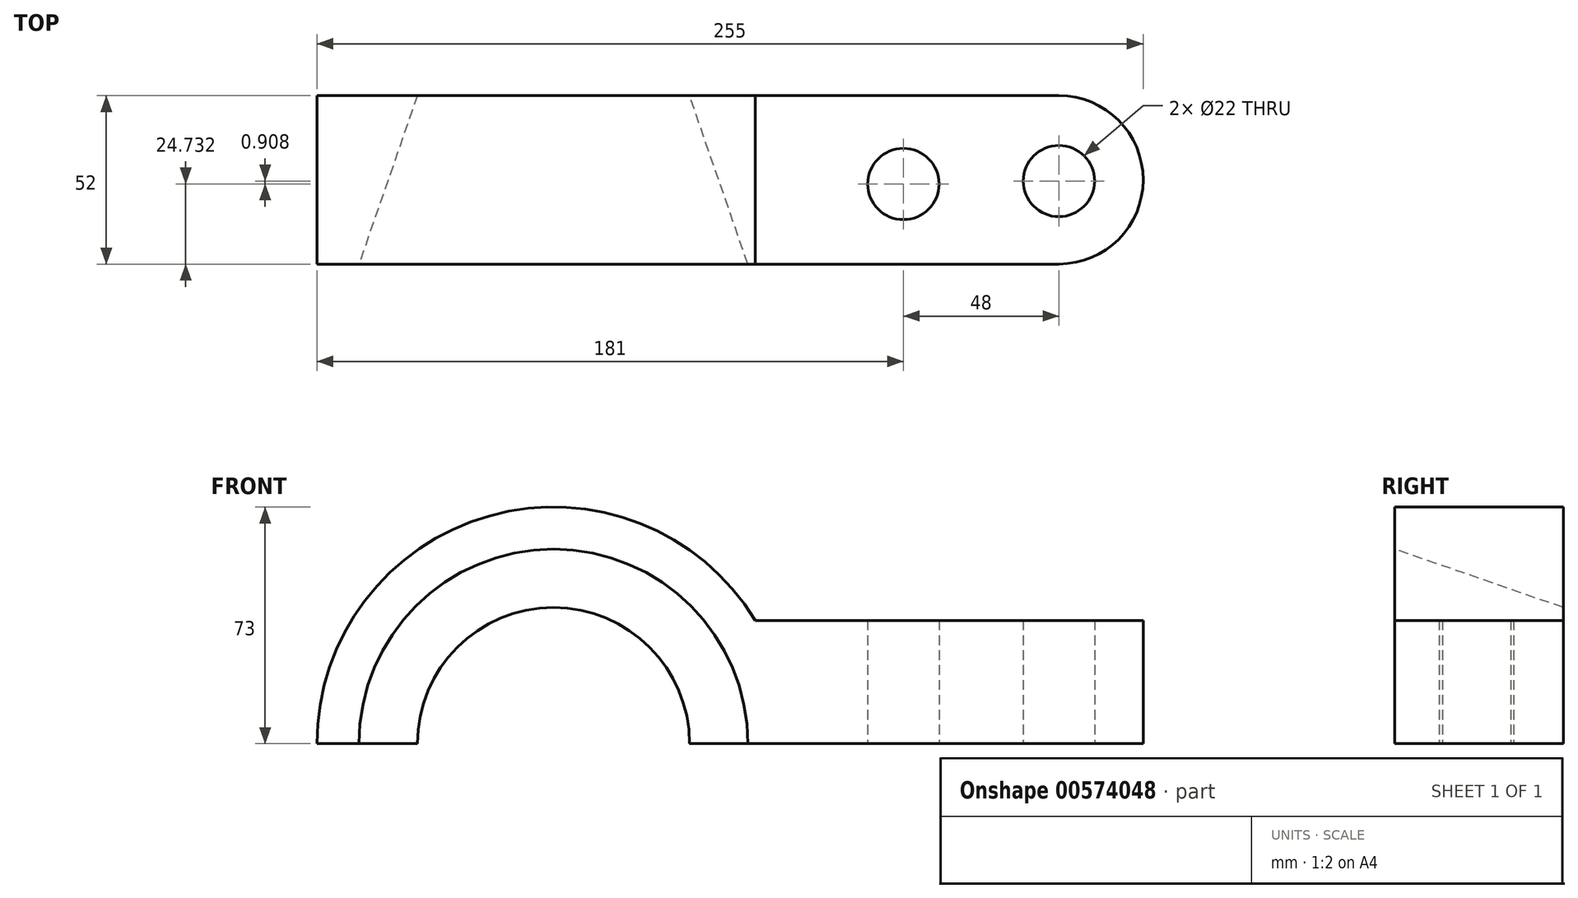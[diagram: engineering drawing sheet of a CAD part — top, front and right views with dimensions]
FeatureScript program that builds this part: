
annotation { "Feature Type Name" : "Feature", "Feature Type Description" : "" }
export const myFeature = defineFeature(function(context is Context, id is Id, definition is map)
    precondition{}
    {
        {
            var Q0;
            Q0=qCreatedBy(makeId("Front.planeOp"),FACE);
            var sketch = newSketch(context, id + "F0", { "sketchPlane" : qUnion([Q0])});
            skArc(sketch, "E0", {"start": v(42, 0) * mm, "mid": v(0, 42) * mm, "end": v(-42, 0) * mm});
            skArc(sketch, "E1", {"start": v(62.33, 38) * mm, "mid": v(-19.73, 70.28) * mm, "end": v(-73, 0) * mm});
            skLineSegment(sketch, "E2", {"start": v(-73, 0) * mm, "end": v(-42, 0) * mm});
            skLineSegment(sketch, "E3.trimOffspring", {"start": v(42, 0) * mm, "end": v(73, 0) * mm});
            skLineSegment(sketch, "E4", {"start": v(62.33, 38) * mm, "end": v(182, 38) * mm});
            skLineSegment(sketch, "E5", {"start": v(182, 38) * mm, "end": v(182, 0) * mm});
            skLineSegment(sketch, "E6", {"start": v(182, 0) * mm, "end": v(73, 0) * mm});
            skSolve(sketch);
        }
        {
            var Q0;
            Q0=makeQuery(id+"F0.imprint","IMPRINT",FACE,{"disambiguationData":[TD([[makeQuery(id+"F0.imprint","IMPRINT",EDGE,{"derivedFrom":sQuery(id+"F0.wireOp",EDGE,"E0")}),-1.0]])]});
            extrude(context, id + "F1", {"entities" : qUnion([Q0]), "depth" : 52 * mm, "offsetDistance" : 25 * mm});
        }
        {
            var Q0;
            Q0=makeQuery(id+"F1.opExtrude","SWEPT_FACE",FACE,{"disambiguationData":[OSD([sQuery(id+"F0.wireOp",EDGE,"E2")])]});
            var sketch = newSketch(context, id + "F2", { "sketchPlane" : qUnion([Q0])});
            skLineSegment(sketch, "E7", {"start": v(-60, 52) * mm, "end": v(-42, 0) * mm});
            skLineSegment(sketch, "E8", {"start": v(-42, 0) * mm, "end": v(-42, 52) * mm});
            skLineSegment(sketch, "E9", {"start": v(-42, 52) * mm, "end": v(-60, 52) * mm});
            skLineSegment(sketch, "E10", {"start": v(0, 53.19) * mm, "end": v(0, 0) * mm});
            skSolve(sketch);
        }
        {
            var Q0;
            Q0 = qSketchRegion(id + "F2", true);
            var Q1;
            Q1=sQuery(id+"F2.wireOp",EDGE,"E10");
            revolve(context, id + "F3", {"operationType" : NewBodyOperationType.REMOVE, "entities" : qUnion([Q0]), "axis" : qUnion([Q1]), "revolveType" : RevolveType.FULL});
        }
        {
            var Q0;
            Q0=makeQuery(id+"F1.opExtrude","SWEPT_FACE",FACE,{"disambiguationData":[OSD([sQuery(id+"F0.wireOp",EDGE,"E3.trimOffspring"),sQuery(id+"F0.wireOp",EDGE,"E6")])]});
            var sketch = newSketch(context, id + "F4", { "sketchPlane" : qUnion([Q0])});
            skSolve(sketch);
        }
        {
            var Q0;
            {var subQ0=sQuery(id+"F0.wireOp",EDGE,"E6");Q0=makeQuery(id+"F4.imprint","IMPRINT",FACE,{"disambiguationData":[TD([[makeQuery(id+"F4.imprint","IMPRINT",EDGE,{"derivedFrom":makeQuery(id+"F1.opExtrude","SWEPT_EDGE",EDGE,{"disambiguationData":[OSD([sQuery(id+"F0.wireOp",EDGE,"E5"),subQ0])]})}),-1.0]])]});}
            var sketch = newSketch(context, id + "F5", { "sketchPlane" : qUnion([Q0])});
            skCircle(sketch, "E11", {"center": v(108, 27.27) * mm, "radius": 11 * mm});
            skCircle(sketch, "E12", {"center": v(156, 26.36) * mm, "radius": 11 * mm});
            skSolve(sketch);
        }
        {
            var Q0;
            Q0=makeQuery(id+"F5.imprint","IMPRINT",FACE,{"disambiguationData":[TD([[makeQuery(id+"F5.imprint","IMPRINT",EDGE,{"derivedFrom":sQuery(id+"F5.wireOp",EDGE,"E12")}),1.0]])]});
            var Q1;
            Q1=makeQuery(id+"F5.imprint","IMPRINT",FACE,{"disambiguationData":[TD([[makeQuery(id+"F5.imprint","IMPRINT",EDGE,{"derivedFrom":sQuery(id+"F5.wireOp",EDGE,"E11")}),1.0]])]});
            extrude(context, id + "F6", {"entities" : qUnion([Q0, Q1]), "operationType" : NewBodyOperationType.REMOVE, "oppositeDirection" : true, "depth" : 50 * mm, "offsetDistance" : 25 * mm});
        }
        {
            var Q0;
            Q0=makeQuery(id+"F1.opExtrude","CAP_EDGE",EDGE,{"disambiguationData":[OSD([sQuery(id+"F0.wireOp",EDGE,"E5")])],"isStart":false});
            var Q1;
            Q1=makeQuery(id+"F1.opExtrude","CAP_EDGE",EDGE,{"disambiguationData":[OSD([sQuery(id+"F0.wireOp",EDGE,"E5")])],"isStart":true});
            fillet(context, id + "F7", {"entities" : qUnion([Q0, Q1]), "radius" : 26 * mm, "tangentPropagation" : true, "allowEdgeOverflow" : false});
        }
    });
